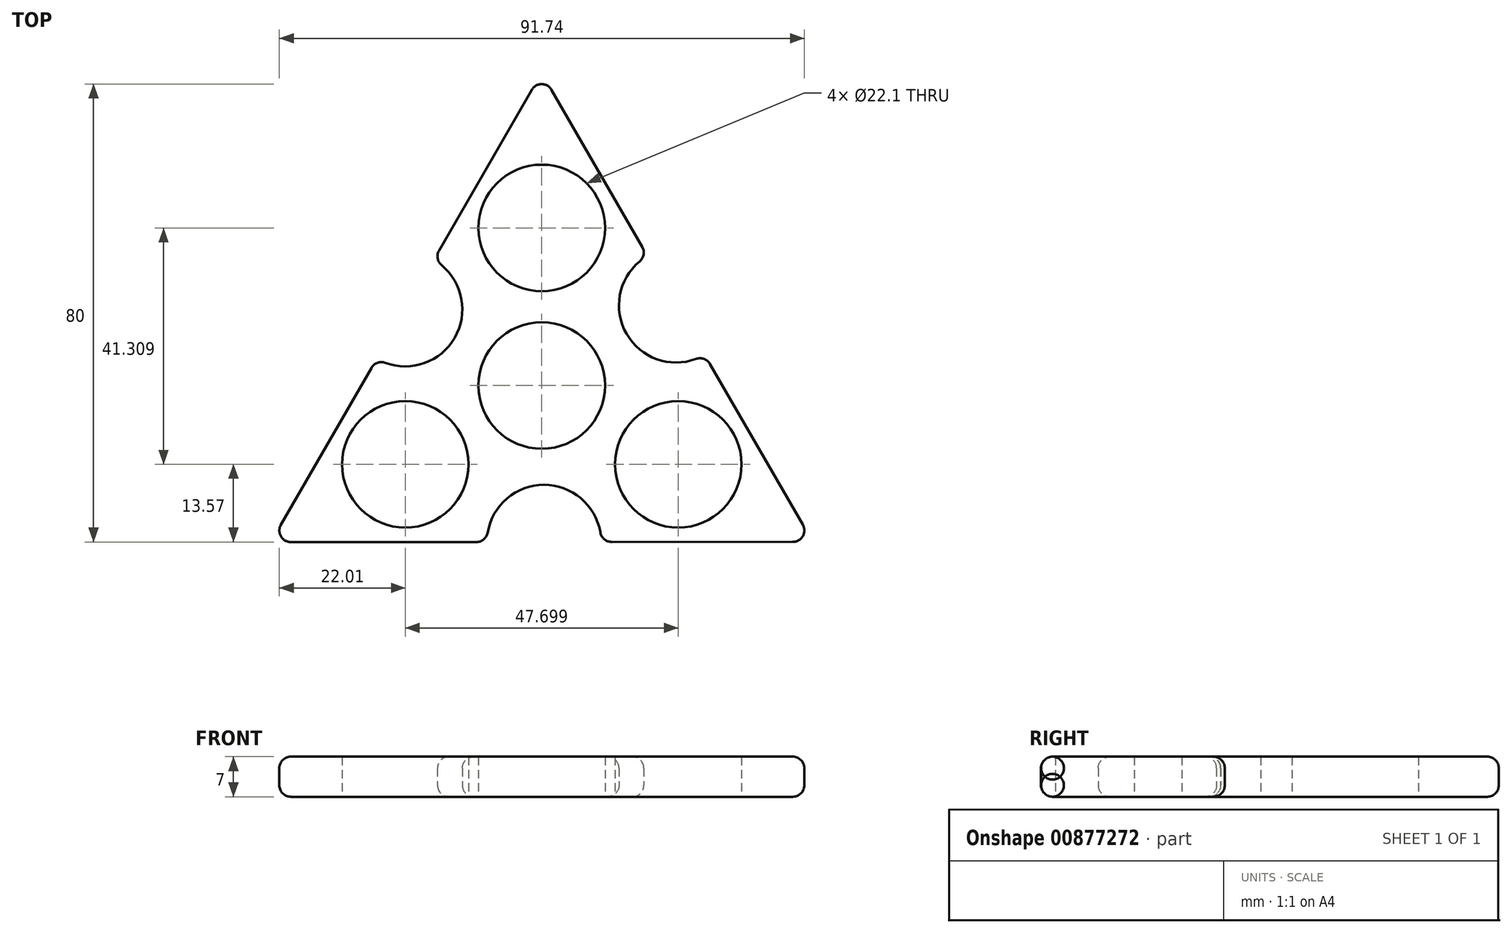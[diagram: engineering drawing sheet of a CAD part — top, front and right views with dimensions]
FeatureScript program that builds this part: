
annotation { "Feature Type Name" : "Feature", "Feature Type Description" : "" }
export const myFeature = defineFeature(function(context is Context, id is Id, definition is map)
    precondition{}
    {
        {
            var Q0;
            Q0=qCreatedBy(makeId("Top.planeOp"),FACE);
            var sketch = newSketch(context, id + "F0", { "sketchPlane" : qUnion([Q0])});
            skCircle(sketch, "E0", {"center": v(0, 0) * mm, "radius": 11.05 * mm});
            skCircle(sketch, "E1", {"center": v(0, 27.54) * mm, "radius": 11.05 * mm});
            skCircle(sketch, "E2.1.0", {"center": v(-23.85, -13.77) * mm, "radius": 11.05 * mm});
            skCircle(sketch, "E2.2.0", {"center": v(23.85, -13.77) * mm, "radius": 11.05 * mm});
            skLineSegment(sketch, "E3", {"start": v(0, 0) * mm, "end": v(46.87, -27.31) * mm, "construction": true});
            skLineSegment(sketch, "E4", {"start": v(0, 0) * mm, "end": v(-57.4, -33.73) * mm, "construction": true});
            skLineSegment(sketch, "E5", {"start": v(0, 0) * mm, "end": v(0, 70.86) * mm, "construction": true});
            skLineSegment(sketch, "E6", {"start": v(-47.32, -27.34) * mm, "end": v(0, 54.69) * mm});
            skLineSegment(sketch, "E7", {"start": v(18.6, 22.72) * mm, "end": v(47.7, -27.31) * mm});
            skArc(sketch, "E8", {"start": v(-28.85, 4.67) * mm, "mid": v(-15.22, 8.33) * mm, "end": v(-18.88, 21.97) * mm});
            skLineSegment(sketch, "E9.1.0", {"start": v(47.7, -27.31) * mm, "end": v(-47.36, -27.34) * mm});
            skLineSegment(sketch, "E9.2.0", {"start": v(-0.02, 54.66) * mm, "end": v(47.34, -27.31) * mm});
            skArc(sketch, "E10.1.0", {"start": v(10.38, -27.32) * mm, "mid": v(0.4, -17.34) * mm, "end": v(-9.59, -27.33) * mm});
            skArc(sketch, "E10.2.0", {"start": v(18.6, 22.72) * mm, "mid": v(14.84, 8.99) * mm, "end": v(28.64, 5.46) * mm});
            skLineSegment(sketch, "E11.trimOffspring", {"start": v(48.13, -28.04) * mm, "end": v(58.95, -34.35) * mm, "construction": true});
            skPoint(sketch, "E12.orphan", {"position": v(48.15, -27.31) * mm});
            skPoint(sketch, "E13.orphan", {"position": v(47.36, -27.34) * mm});
            skPoint(sketch, "E14.orphan", {"position": v(-47.73, -28.04) * mm});
            skPoint(sketch, "E15.orphan", {"position": v(-0.42, 55.36) * mm});
            skSolve(sketch);
        }
        {
            var Q0;
            Q0=makeQuery(id+"F0.imprint","IMPRINT",FACE,{"disambiguationData":[TD([[makeQuery(id+"F0.imprint","IMPRINT",EDGE,{"derivedFrom":sQuery(id+"F0.wireOp",EDGE,"E0")}),-1.0]])]});
            extrude(context, id + "F1", {"entities" : qUnion([Q0]), "depth" : 7 * mm, "offsetDistance" : 25 * mm});
        }
        {
            var Q0;
            {var subQ0=sQuery(id+"F0.wireOp",EDGE,"E6");Q0=makeQuery(id+"F1.opExtrude","CAP_EDGE",EDGE,{"disambiguationData":[OSD([subQ0]),TDD([makeQuery(id+"F0.imprint","IMPRINT",EDGE,{"disambiguationData":[TD([[makeQuery(id+"F0.imprint","INTERSECT",VERTEX,{"derivedFrom":[subQ0,sQuery(id+"F0.wireOp",EDGE,"E9.1.0")]}),-1.0]])],"derivedFrom":subQ0})])],"isStart":false});}
            var Q1;
            {var subQ0=sQuery(id+"F0.wireOp",EDGE,"E6");Q1=makeQuery(id+"F1.opExtrude","CAP_EDGE",EDGE,{"disambiguationData":[OSD([subQ0]),TDD([makeQuery(id+"F0.imprint","IMPRINT",EDGE,{"disambiguationData":[TD([[makeQuery(id+"F0.imprint","INTERSECT",VERTEX,{"derivedFrom":[subQ0,sQuery(id+"F0.wireOp",EDGE,"E9.1.0")]}),-1.0]])],"derivedFrom":subQ0})])],"isStart":true});}
            var Q2;
            {var subQ0=sQuery(id+"F0.wireOp",EDGE,"E6");Q2=makeQuery(id+"F1.opExtrude","CAP_EDGE",EDGE,{"disambiguationData":[OSD([subQ0]),TDD([makeQuery(id+"F0.imprint","IMPRINT",EDGE,{"disambiguationData":[TD([[makeQuery(id+"F0.imprint","INTERSECT",VERTEX,{"disambiguationData":[OD(1.0)],"derivedFrom":[subQ0,sQuery(id+"F0.wireOp",EDGE,"E8")]}),-1.0]])],"derivedFrom":subQ0})])],"isStart":false});}
            var Q3;
            {var subQ0=sQuery(id+"F0.wireOp",EDGE,"E6");Q3=makeQuery(id+"F1.opExtrude","CAP_EDGE",EDGE,{"disambiguationData":[OSD([subQ0]),TDD([makeQuery(id+"F0.imprint","IMPRINT",EDGE,{"disambiguationData":[TD([[makeQuery(id+"F0.imprint","INTERSECT",VERTEX,{"disambiguationData":[OD(1.0)],"derivedFrom":[subQ0,sQuery(id+"F0.wireOp",EDGE,"E8")]}),-1.0]])],"derivedFrom":subQ0})])],"isStart":true});}
            var Q4;
            {var subQ0=sQuery(id+"F0.wireOp",EDGE,"E9.2.0");Q4=makeQuery(id+"F1.opExtrude","CAP_EDGE",EDGE,{"disambiguationData":[OSD([subQ0]),TDD([makeQuery(id+"F0.imprint","IMPRINT",EDGE,{"disambiguationData":[TD([[makeQuery(id+"F0.imprint","INTERSECT",VERTEX,{"derivedFrom":[sQuery(id+"F0.wireOp",EDGE,"E6"),subQ0]}),-1.0]])],"derivedFrom":subQ0})])],"isStart":true});}
            var Q5;
            {var subQ0=sQuery(id+"F0.wireOp",EDGE,"E9.2.0");Q5=makeQuery(id+"F1.opExtrude","CAP_EDGE",EDGE,{"disambiguationData":[OSD([subQ0]),TDD([makeQuery(id+"F0.imprint","IMPRINT",EDGE,{"disambiguationData":[TD([[makeQuery(id+"F0.imprint","INTERSECT",VERTEX,{"derivedFrom":[sQuery(id+"F0.wireOp",EDGE,"E6"),subQ0]}),-1.0]])],"derivedFrom":subQ0})])],"isStart":false});}
            var Q6;
            {var subQ0=sQuery(id+"F0.wireOp",EDGE,"E9.1.0");Q6=makeQuery(id+"F1.opExtrude","CAP_EDGE",EDGE,{"disambiguationData":[OSD([subQ0]),TDD([makeQuery(id+"F0.imprint","IMPRINT",EDGE,{"disambiguationData":[TD([[makeQuery(id+"F0.imprint","INTERSECT",VERTEX,{"derivedFrom":[sQuery(id+"F0.wireOp",EDGE,"E6"),subQ0]}),1.0]])],"derivedFrom":subQ0})])],"isStart":true});}
            var Q7;
            {var subQ0=sQuery(id+"F0.wireOp",EDGE,"E9.1.0");Q7=makeQuery(id+"F1.opExtrude","SWEPT_FACE",FACE,{"disambiguationData":[OSD([subQ0]),TDD([makeQuery(id+"F0.imprint","IMPRINT",EDGE,{"disambiguationData":[TD([[makeQuery(id+"F0.imprint","INTERSECT",VERTEX,{"derivedFrom":[sQuery(id+"F0.wireOp",EDGE,"E6"),subQ0]}),1.0]])],"derivedFrom":subQ0})])]});}
            var Q8;
            {var subQ0=sQuery(id+"F0.wireOp",EDGE,"E9.1.0");Q8=makeQuery(id+"F1.opExtrude","SWEPT_FACE",FACE,{"disambiguationData":[OSD([subQ0]),TDD([makeQuery(id+"F0.imprint","IMPRINT",EDGE,{"disambiguationData":[TD([[makeQuery(id+"F0.imprint","INTERSECT",VERTEX,{"derivedFrom":[subQ0,sQuery(id+"F0.wireOp",EDGE,"E9.2.0")]}),-1.0]])],"derivedFrom":subQ0})])]});}
            var Q9;
            {var subQ0=sQuery(id+"F0.wireOp",EDGE,"E8");var subQ1=sQuery(id+"F0.wireOp",EDGE,"E6");Q9=makeQuery(id+"F1.opExtrude","SWEPT_EDGE",EDGE,{"disambiguationData":[OSD([subQ1,subQ0]),TDD([makeQuery(id+"F0.imprint","INTERSECT",VERTEX,{"disambiguationData":[OD(1.0)],"derivedFrom":[subQ1,subQ0]})])]});}
            var Q10;
            Q10=makeQuery(id+"F1.opExtrude","SWEPT_EDGE",EDGE,{"disambiguationData":[OSD([sQuery(id+"F0.wireOp",EDGE,"E6"),sQuery(id+"F0.wireOp",EDGE,"E9.2.0")])]});
            var Q11;
            {var subQ0=sQuery(id+"F0.wireOp",EDGE,"E10.2.0");var subQ1=sQuery(id+"F0.wireOp",EDGE,"E9.2.0");Q11=makeQuery(id+"F1.opExtrude","SWEPT_EDGE",EDGE,{"disambiguationData":[OSD([subQ1,subQ0]),TDD([makeQuery(id+"F0.imprint","INTERSECT",VERTEX,{"disambiguationData":[OD(0.0)],"derivedFrom":[subQ1,subQ0]})])]});}
            var Q12;
            {var subQ0=sQuery(id+"F0.wireOp",EDGE,"E10.2.0");var subQ1=sQuery(id+"F0.wireOp",EDGE,"E9.2.0");Q12=makeQuery(id+"F1.opExtrude","SWEPT_EDGE",EDGE,{"disambiguationData":[OSD([subQ1,subQ0]),TDD([makeQuery(id+"F0.imprint","INTERSECT",VERTEX,{"disambiguationData":[OD(1.0)],"derivedFrom":[subQ1,subQ0]})])]});}
            var Q13;
            {var subQ0=sQuery(id+"F0.wireOp",EDGE,"E9.2.0");Q13=makeQuery(id+"F1.opExtrude","SWEPT_FACE",FACE,{"disambiguationData":[OSD([subQ0]),TDD([makeQuery(id+"F0.imprint","IMPRINT",EDGE,{"disambiguationData":[TD([[makeQuery(id+"F0.imprint","INTERSECT",VERTEX,{"derivedFrom":[sQuery(id+"F0.wireOp",EDGE,"E9.1.0"),subQ0]}),1.0]])],"derivedFrom":subQ0})])]});}
            var Q14;
            {var subQ0=sQuery(id+"F0.wireOp",EDGE,"E8");var subQ1=sQuery(id+"F0.wireOp",EDGE,"E6");Q14=makeQuery(id+"F1.opExtrude","SWEPT_EDGE",EDGE,{"disambiguationData":[OSD([subQ1,subQ0]),TDD([makeQuery(id+"F0.imprint","INTERSECT",VERTEX,{"disambiguationData":[OD(0.0)],"derivedFrom":[subQ1,subQ0]})])]});}
            fillet(context, id + "F2", {"entities" : qUnion([Q0, Q1, Q2, Q3, Q4, Q5, Q6, Q7, Q8, Q9, Q10, Q11, Q12, Q13, Q14]), "radius" : 2 * mm, "tangentPropagation" : true, "allowEdgeOverflow" : false});
        }
        {
            var Q0;
            Q0=makeQuery(id+"F1.opExtrude","SWEPT_FACE",FACE,{"disambiguationData":[OSD([sQuery(id+"F0.wireOp",EDGE,"E8")])]});
            var Q1;
            Q1=makeQuery(id+"F1.opExtrude","CAP_EDGE",EDGE,{"disambiguationData":[OSD([sQuery(id+"F0.wireOp",EDGE,"E10.2.0")])],"isStart":false});
            var Q2;
            Q2=makeQuery(id+"F1.opExtrude","SWEPT_FACE",FACE,{"disambiguationData":[OSD([sQuery(id+"F0.wireOp",EDGE,"E10.2.0")])]});
            var Q3;
            Q3=makeQuery(id+"F1.opExtrude","SWEPT_FACE",FACE,{"disambiguationData":[OSD([sQuery(id+"F0.wireOp",EDGE,"E10.1.0")])]});
            fillet(context, id + "F3", {"entities" : qUnion([Q0, Q1, Q2, Q3]), "radius" : 2 * mm, "tangentPropagation" : true, "allowEdgeOverflow" : false});
        }
    });
